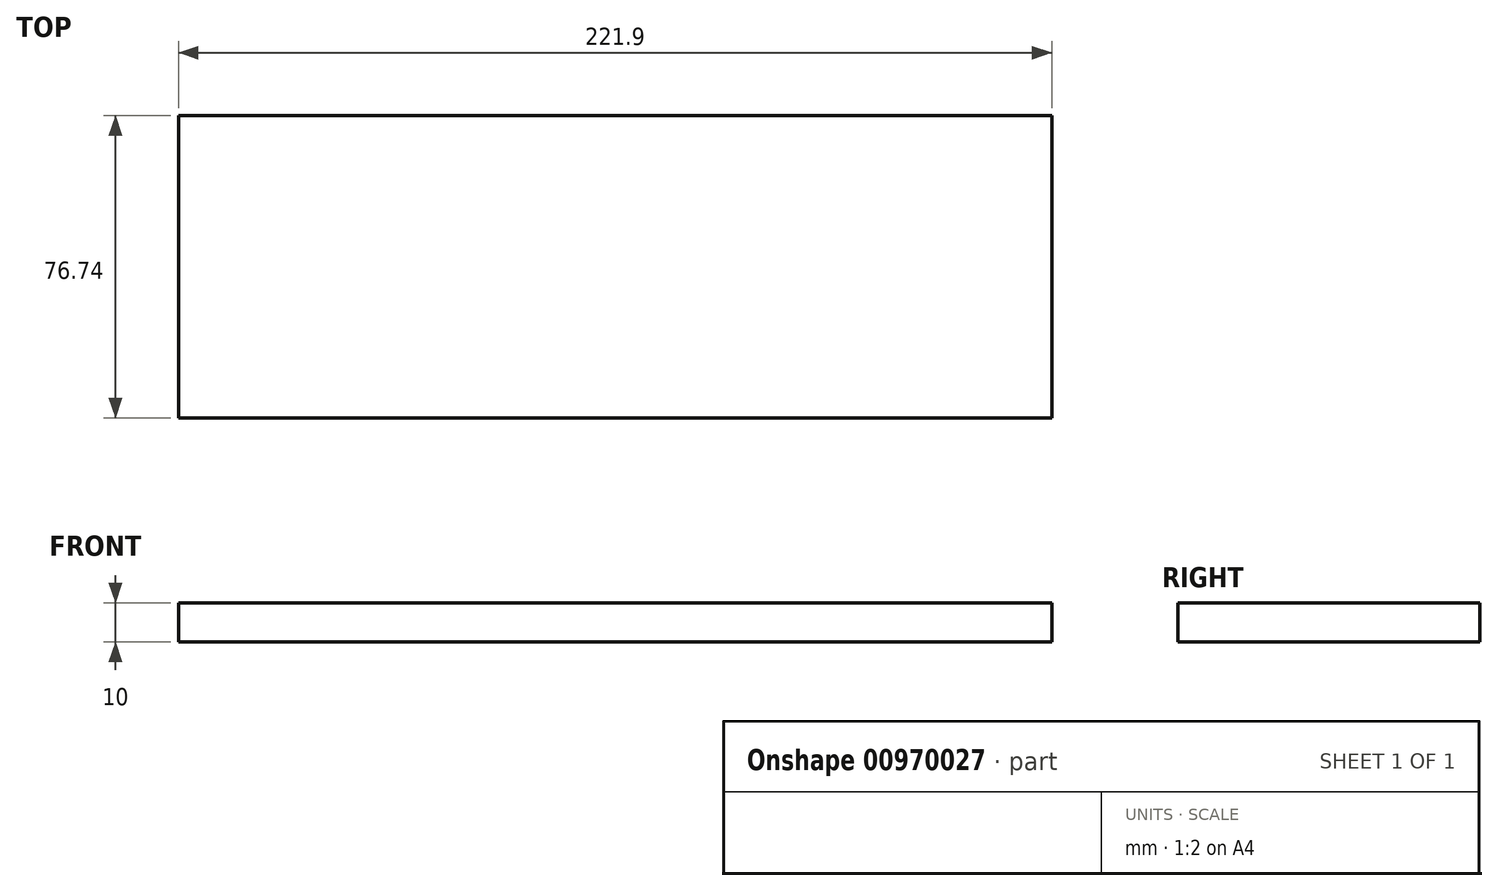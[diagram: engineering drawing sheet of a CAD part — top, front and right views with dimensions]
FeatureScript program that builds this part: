
annotation { "Feature Type Name" : "Feature", "Feature Type Description" : "" }
export const myFeature = defineFeature(function(context is Context, id is Id, definition is map)
    precondition{}
    {
        {
            var Q0;
            Q0=qCreatedBy(makeId("Top.planeOp"),FACE);
            var sketch = newSketch(context, id + "F0", { "sketchPlane" : qUnion([Q0])});
            skLineSegment(sketch, "E0", {"start": v(-70.68, 27.65) * mm, "end": v(-70.68, -49.1) * mm});
            skLineSegment(sketch, "E1", {"start": v(-70.68, 27.65) * mm, "end": v(151.22, 27.65) * mm});
            skLineSegment(sketch, "E2", {"start": v(151.22, 27.65) * mm, "end": v(151.22, -49.1) * mm});
            skLineSegment(sketch, "E3", {"start": v(151.22, -49.1) * mm, "end": v(-70.68, -49.1) * mm});
            skSolve(sketch);
        }
        {
            var Q0;
            Q0=makeQuery(id+"F0.imprint","IMPRINT",FACE,{"disambiguationData":[TD([[makeQuery(id+"F0.imprint","IMPRINT",EDGE,{"derivedFrom":sQuery(id+"F0.wireOp",EDGE,"E0")}),1.0]])]});
            extrude(context, id + "F1", {"entities" : qUnion([Q0]), "depth" : 10 * mm, "offsetDistance" : 25 * mm});
        }
    });
